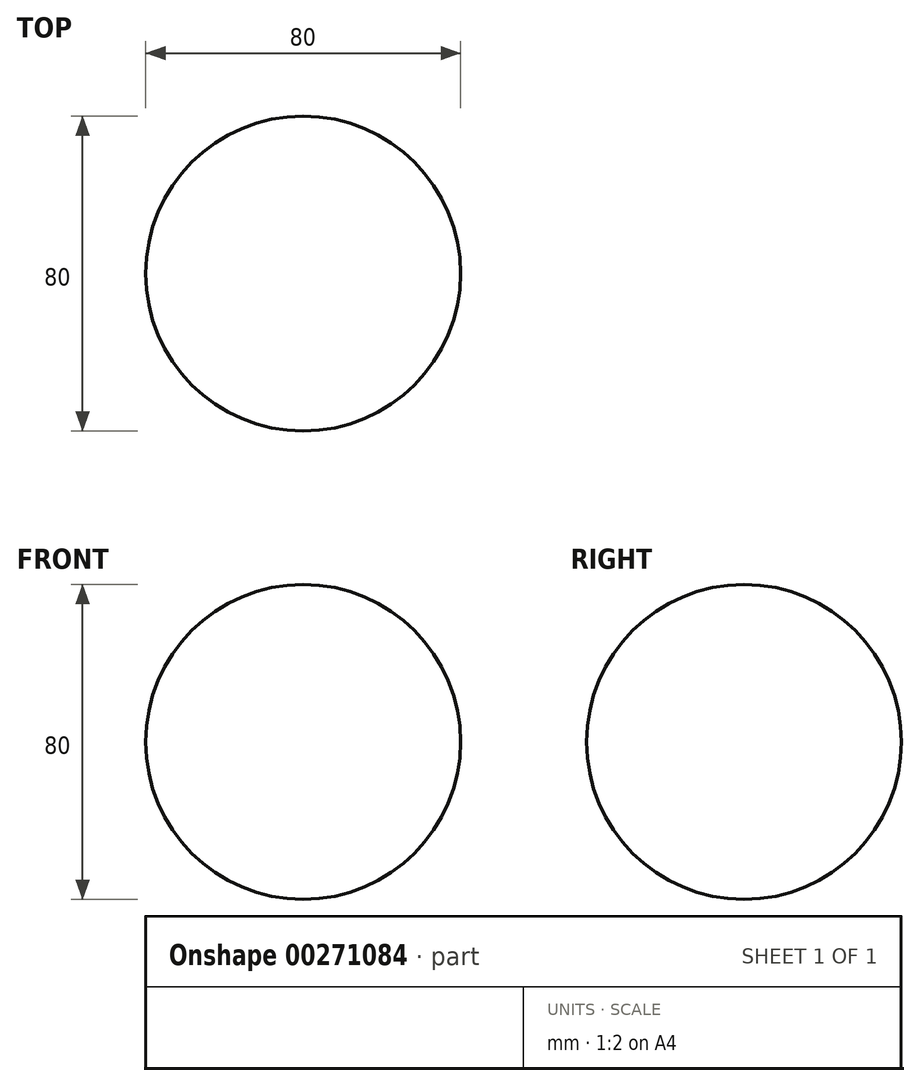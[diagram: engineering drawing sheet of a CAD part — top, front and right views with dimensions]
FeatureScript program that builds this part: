
annotation { "Feature Type Name" : "Feature", "Feature Type Description" : "" }
export const myFeature = defineFeature(function(context is Context, id is Id, definition is map)
    precondition{}
    {
        {
            var Q0;
            Q0=qCreatedBy(makeId("Front.planeOp"),FACE);
            var sketch = newSketch(context, id + "F0", { "sketchPlane" : qUnion([Q0])});
            skLineSegment(sketch, "E0", {"start": v(0, 40) * mm, "end": v(0, -40) * mm});
            skArc(sketch, "E1", {"start": v(0, 40) * mm, "mid": v(40, 0) * mm, "end": v(0, -40) * mm});
            skLineSegment(sketch, "E2", {"start": v(0, 61.07) * mm, "end": v(0, -56.1) * mm, "construction": true});
            skSolve(sketch);
        }
        {
            var Q0;
            Q0=makeQuery(id+"F0.imprint","IMPRINT",FACE,{"disambiguationData":[TD([[makeQuery(id+"F0.imprint","IMPRINT",EDGE,{"derivedFrom":sQuery(id+"F0.wireOp",EDGE,"E0")}),1.0]])]});
            var Q1;
            Q1=sQuery(id+"F0.wireOp",EDGE,"E2");
            revolve(context, id + "F1", {"entities" : qUnion([Q0]), "axis" : qUnion([Q1]), "revolveType" : RevolveType.FULL});
        }
    });
